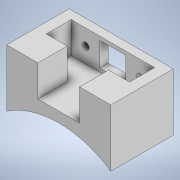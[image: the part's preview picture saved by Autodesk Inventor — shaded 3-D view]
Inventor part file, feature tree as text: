
AUTODESK INVENTOR PART (.ipt)
format: ipt  version: 2022.2 (Build 262287000, 287)  size: 866,816 bytes
history: native  units: mm
features: sketch x5, extrude x3, hole x1, plane x1, emboss x1
ambient origin geometry x8: Origin, YZ Plane, XZ Plane, XY Plane, X Axis, Y Axis, Z Axis, Center Point
bodies: Solid1 (feature_tree)
feature tree (11):
  extrude  "Extrusion1"  Depth=50.0mm
  extrude  "Extrusion2"  Depth=30.0mm TaperAngle=0.0deg
  extrude  "Extrusion3"  Depth=14.0mm
  hole  "Hole1"  [1 undecoded]
  plane  "Work Plane2"
  emboss  "Emboss1"
  sketch  "Sketch1"  dims[d0=90.0mm d1=50.0mm]
  sketch  "Sketch2"  dims[d2=5.0mm d3=30.0mm d4=0.0mm]
  sketch  "Sketch3"  dims[d5=20.0mm d6=14.0mm]
  sketch  "Sketch5"  dims[d7=40.0mm d8=12.0mm]
  sketch  "Sketch6"  dims[d9=4.0mm d10=15.0mm d11=0.0mm d12=11.5mm d13=12.5mm d14=15.0mm d15=0.0mm d16=26.0mm d17=3.264mm d18=6.0mm d19=5.715mm d20=2.0mm d21=14.3117mm d22=8.0mm d23=20.594885mm d24=50.0mm d25=1.0mm d26=0.0mm]
note: 1 required parameter value undecoded (feature->parameter linkage not recoverable at this tier; creation-order binding heuristic only, values carry confidence <= 0.55)
